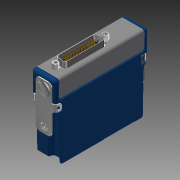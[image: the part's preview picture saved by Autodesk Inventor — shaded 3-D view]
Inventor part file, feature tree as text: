
AUTODESK INVENTOR PART (.ipt)
format: ipt  version: 2013 (Build 170138000, 138)  size: 8,072,192 bytes
history: native  units: mm
features: other x3, extrude x3, sketch x2, imported_body x1, fillet x1
ambient origin geometry x8: Origin, YZ Plane, XZ Plane, XY Plane, X Axis, Y Axis, Z Axis, Center Point
bodies: Solid1 (feature_tree)
feature tree (10):
  imported_body  "Base1"
  other  "RIGHT"
  other  "TOP"
  other  "FRONT"
  sketch  "Sketch3"  dims[d22=5.08mm d23=0.0mm]
  extrude  "Extrusion2"  Depth=1.27mm TaperAngle=0.0deg
  extrude  "Extrusion3"  [1 undecoded]
  sketch  "Sketch2"  dims[d0=25.4mm d1=2.54mm d3=10.0mm d5=130.0mm d6=25.4mm d7=2.54mm d9=10.0mm d11=120.0mm d12=1.397mm d13=1.397mm d14=1.27mm d15=1.008245mm d17=0.0mm d18=25.4mm d19=0.381mm d20=1.27mm d21=0.0mm]
  fillet  "Fillet1"  [1 undecoded]
  extrude  "Extrusion1"  [1 undecoded]
note: 3 required parameter values undecoded (feature->parameter linkage not recoverable at this tier; creation-order binding heuristic only, values carry confidence <= 0.55)
